# Revit family: irnes WALMDACH PR  60 MIT ZARGE
name_source: partatom
category: Windows
revit_build: Autodesk Revit 2014 (Build: 20130308_1515(x64)
units: mm (PartAtom-declared; Revit-internal decimal feet)

## types (1)
- irnes WALMDACH PR  60 MIT ZARGE
    Analytic Construction = <None>
    BIMobject category_2 = Roof Window
    Date of publishing = 2014-01-01
    Depth = 0.00
    Design country = Germany
    Edition number = 1
    Environmental product declaration = EN 15804
    Glass Type = Double glazing (thickness 32mm)
    IFC Classification = Roof
    Insulation = Cavity_Lamilux_Fill
    Jambs and transoms heat transfer coefficient = 1.3 to 0.72 W/m2k
    Manufacturer country = Germany
    Manufacturer name = LAMILUX
    Material Main = Lamilux-White
    Material Secondary = Lamilux- Glass
    NBS Reference Code = 25-10-20
    NBS Reference Description = Curtain Walling Systems
    Nominal height = 0.00
    Nominal width = 0.00
    Permeability to air = Class 4 EN 12207
    Product SKU = Lamilux_PR60
    Product data url = http://lamilux.bimobject.com
    Product family = Daylight element
    Product group = Continuous Rooflight
    QR code = http://lamilux.bimobject.com
    Rwp_dB = 38 dB
    UNSPSC Code = 30151806
    Ug-value = 1,0 W/m2K
    Uniclass 1.4 Code = L414
    Uniclass 1.4 Description = Rooflights
    Uniclass 2.0 Code = SS-25-10-20
    Uniclass 2.0 Description = Curtain Walling Systems
    Visual Transmission = 70%
    Watertightness = Class E 1200 EN 12208
    Weight Net (Kg) = 0
    Wind Load Resistancy = Class C4-B5 EN 12210
    g-Value = 44%

## geometry (parser evidence)
native form markers: Sweep x14
no freeform markers — native parametric forms only
